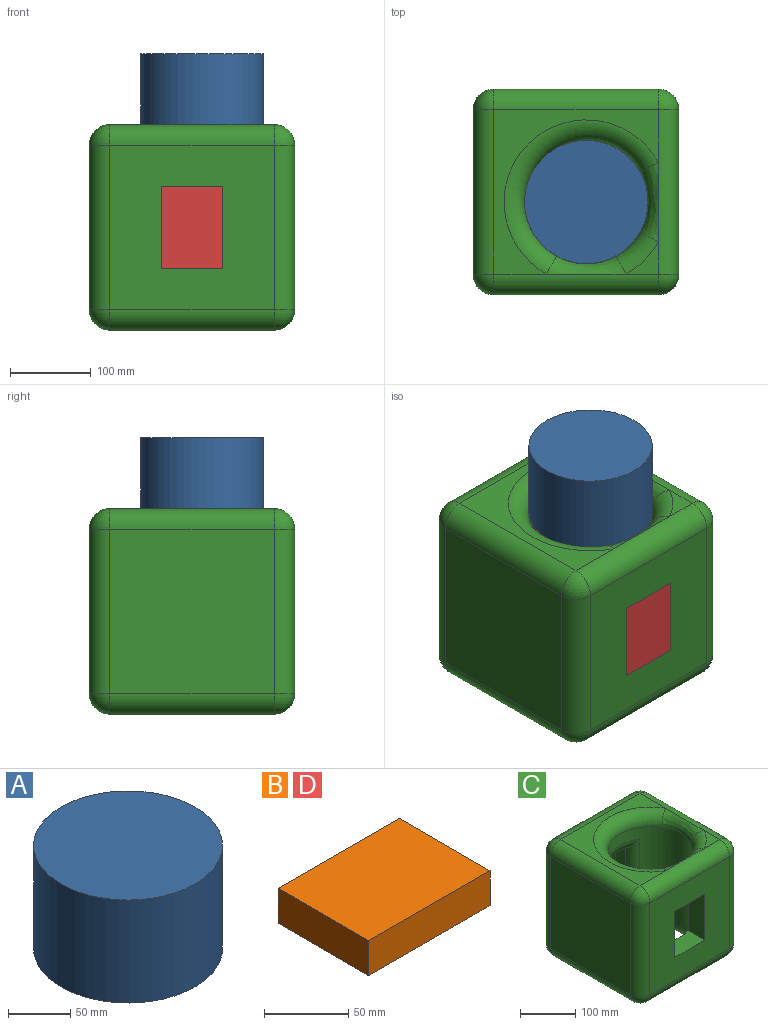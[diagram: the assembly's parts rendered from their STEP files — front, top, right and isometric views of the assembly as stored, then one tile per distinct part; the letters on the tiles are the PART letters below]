
ASSEMBLY  parts=4 mates=3
PART A: 3 faces, bbox 152.4x152.4x101.6 mm
  f0: cylinder r=76.2mm len=152.4mm, axis (0,0,-1), area 48643.9mm2, adj f1,f2
  f1: plane 152.4x152.4mm, normal (0,0,1), area 18241.5mm2, adj f0
  f2: plane 152.4x152.4mm, normal (0,0,-1), area 18241.5mm2, adj f0
PART B: 6 faces, bbox 101.6x76.2x25.4 mm
  f0: plane 76.2x25.4mm, normal (1,0,0), area 1935.5mm2, adj f1,f3,f4,f5
  f1: plane 101.6x25.4mm, normal (0,1,0), area 2580.6mm2, adj f0,f2,f4,f5
  f2: plane 76.2x25.4mm, normal (-1,0,0), area 1935.5mm2, adj f1,f3,f4,f5
  f3: plane 101.6x25.4mm, normal (0,-1,0), area 2580.6mm2, adj f0,f2,f4,f5
  f4: plane 101.6x76.2mm, normal (0,0,1), area 7741.9mm2, adj f0,f1,f2,f3
  f5: plane 101.6x76.2mm, normal (0,0,-1), area 7741.9mm2, adj f0,f1,f2,f3
PART C: 53 faces, bbox 254.5x254.5x258.8 mm
  f0: plane 203.2x203.2mm, normal (0,1,0), area 21935.4mm2, adj f14,f23,f24,f28,f49,f50,f51,f52
  f1: plane 203.2x203.2mm, normal (0,-1,0), area 33548.3mm2, adj f9,f12,f16,f17,f37,f38,f39,f40
  f2: cylinder r=76.2mm len=210.01mm, axis (0,0,1), area 73624.5mm2, adj f29,f30,f31,f32,f33,f34,f35,f36
  f3: plane 39.71x39.71mm, normal (0,0,1), area 639.8mm2, adj f12,f22,f34
  f4: plane 203.2x203.2mm, normal (0,0,-1), area 9909mm2, adj f15,f16,f24,f25,f31
  f5: plane 203.2x203.2mm, normal (1,0,0), area 41290.2mm2, adj f17,f22,f25,f28
  f6: plane 203.2x203.2mm, normal (-1,0,0), area 41290.2mm2, adj f9,f13,f14,f15
  f7: plane 203.2x203.2mm, normal (0,0,1), area 9909mm2, adj f12,f13,f22,f23,f35
  f8: plane 39.71x39.71mm, normal (0,0,-1), area 639.8mm2, adj f16,f25,f30
  f9: cylinder r=25.4mm len=203.2mm, axis (0,0,1), area 8107.3mm2, adj f1,f6,f10,f11
  f10: sphere r=25.4mm, area 1013.4mm2, adj f9,f12,f13
  f11: sphere r=25.4mm, area 1013.4mm2, adj f9,f15,f16
  f12: cylinder r=25.4mm len=203.2mm, axis (-1,0,0), area 8107.3mm2, adj f1,f3,f7,f10,f18,f33
  f13: cylinder r=25.4mm len=203.2mm, axis (0,1,0), area 8107.3mm2, adj f6,f7,f10,f19
  f14: cylinder r=25.4mm len=203.2mm, axis (0,0,-1), area 8107.3mm2, adj f0,f6,f19,f20
  f15: cylinder r=25.4mm len=203.2mm, axis (0,-1,0), area 8107.3mm2, adj f4,f6,f11,f20
  f16: cylinder r=25.4mm len=203.2mm, axis (1,0,0), area 8107.3mm2, adj f1,f4,f8,f11,f21,f29
  f17: cylinder r=25.4mm len=203.2mm, axis (0,0,-1), area 8107.3mm2, adj f1,f5,f18,f21
  f18: sphere r=25.4mm, area 1013.4mm2, adj f12,f17,f22
  f19: sphere r=25.4mm, area 1013.4mm2, adj f13,f14,f23
  f20: sphere r=25.4mm, area 1013.4mm2, adj f14,f15,f24
  f21: sphere r=25.4mm, area 1013.4mm2, adj f16,f17,f25
  f22: cylinder r=25.4mm len=203.2mm, axis (0,-1,0), area 8107.3mm2, adj f3,f5,f7,f18,f26,f36
  f23: cylinder r=25.4mm len=203.2mm, axis (1,0,0), area 8107.3mm2, adj f0,f7,f19,f26
  f24: cylinder r=25.4mm len=203.2mm, axis (-1,0,0), area 8107.3mm2, adj f0,f4,f20,f27
  f25: cylinder r=25.4mm len=203.2mm, axis (0,1,0), area 8107.3mm2, adj f4,f5,f8,f21,f27,f32
  f26: sphere r=25.4mm, area 1013.4mm2, adj f22,f23,f28
  f27: sphere r=25.4mm, area 1013.4mm2, adj f24,f25,f28
  f28: cylinder r=25.4mm len=203.2mm, axis (0,0,1), area 8107.3mm2, adj f0,f5,f26,f27
  f29: bspline ~104.77x27.55mm, area 2583.6mm2, adj f2,f16,f30,f31
  f30: torus R=101.6mm, axis (0,0,1), area 1909mm2, adj f2,f8,f29,f32
  f31: torus R=101.6mm, axis (0,0,1), area 12617.1mm2, adj f2,f4,f29,f32
  f32: bspline ~104.77x27.55mm, area 2583.6mm2, adj f2,f25,f30,f31
  f33: bspline ~104.77x27.55mm, area 2583.6mm2, adj f2,f12,f34,f35
  f34: torus R=101.6mm, axis (0,0,1), area 1909mm2, adj f2,f3,f33,f36
  f35: torus R=101.6mm, axis (0,0,1), area 12617.1mm2, adj f2,f7,f33,f36
  f36: bspline ~104.77x27.55mm, area 2583.6mm2, adj f2,f22,f34,f35
  f37: plane 101.6x57.5mm, normal (1,0,0), area 5842.4mm2, adj f1,f2,f38,f40
  f38: plane 76.2x57.5mm, normal (0,0,1), area 3249.5mm2, adj f1,f2,f37,f39
  f39: plane 101.6x42.46mm, normal (-1,0,0), area 4313.7mm2, adj f1,f2,f38,f40
  f40: plane 76.2x57.5mm, normal (0,0,-1), area 3249.5mm2, adj f1,f2,f37,f39
  f41: plane 76.2x26.31mm, normal (0,0,-1), area 1218.8mm2, adj f42,f44,f48,f49
  f42: plane 105.81x26.4mm, normal (-1,0,0), area 2687.3mm2, adj f41,f43,f45,f46,f48,f50
  f43: plane 76.2x26.31mm, normal (0,0,1), area 1218.8mm2, adj f42,f44,f45,f52
  f44: plane 115.79x47.57mm, normal (1,0,0), area 4876.3mm2, adj f41,f43,f45,f47,f48,f51
  f45: torus R=101.6mm, axis (0,0,-1), area 3415.1mm2, adj f2,f42,f43,f44,f46,f47
  f46: cylinder r=25.4mm len=152.4mm, axis (0,0,1), area 3340.7mm2, adj f2,f42,f45,f48
  f47: cylinder r=25.4mm len=152.4mm, axis (0,0,1), area 2433.7mm2, adj f2,f44,f45,f48
  f48: torus R=101.6mm, axis (0,0,-1), area 3412.3mm2, adj f2,f41,f42,f44,f46,f47
  f49: cylinder r=25.4mm len=127mm, axis (1,0,0), area 3776.8mm2, adj f0,f41,f50,f51
  f50: cylinder r=25.4mm len=152.4mm, axis (0,0,-1), area 4790.2mm2, adj f0,f42,f49,f52
  f51: cylinder r=25.4mm len=152.4mm, axis (0,0,1), area 4790.2mm2, adj f0,f44,f49,f52
  f52: cylinder r=25.4mm len=127mm, axis (-1,0,0), area 3776.8mm2, adj f0,f43,f50,f51
PART D: same geometry as B
PLACE A rot(axis=(1,0,0),180deg) t=(12.7,-12.7,341.35)mm
PLACE B rot(axis=(-0.58,-0.58,-0.58),120deg) t=(0,88.9,132.15)mm
PLACE C at identity fixed
PLACE D rot(axis=(-0.58,-0.58,-0.58),120deg) t=(0,-127,127)mm
MATE slider A.f0 <-> C.f2  axis (0,0,-1) through (12.7,-12.7,239.75)mm
MATE slider C.f41 <-> B.f0  axis (0,0,-1) through (0,101.6,177.8)mm
MATE fastened D.f5 <-> C.f1  axis (0,-1,0) through (0,-127,127)mm
